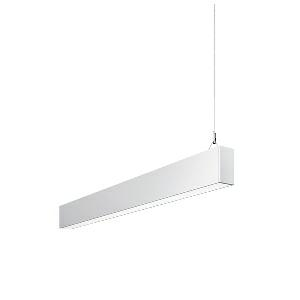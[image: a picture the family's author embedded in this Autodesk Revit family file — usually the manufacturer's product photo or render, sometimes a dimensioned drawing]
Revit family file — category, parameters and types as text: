
# Revit family: idoo_line_-_ilp_3000_vtl_d_end_00806451_e8ea
name_source: partatom
category: Lighting Fixtures
units: mm (PartAtom-declared; Revit-internal decimal feet)

## family parameters
Cut with Voids When Loaded = No
Host = Face
Light Source = No
Part Type = Normal
Room Calculation Point = No
Round Connector Dimension = Use Diameter
Shared = No

## types (1)
- IDOO.line - ILP 3000/VTL/D END (1 x LED, 3150 lm, 2700-6500K)
    Apparent Load = 32 VA
    Approval mark = CE
    CIE Flux Codes = 66 91 98 40 100
    Color Rendering = 90-100
    Color Temperature = 2700-6500K
    Control Gear = Electronic ballast
    Default Elevation = 1800 mm
    Description = ILP 3000/VTL/D|Suspended luminaire|light source: LED|connected load: 220-240 V, 50/60 Hz|Power consumption: approx. 32 W|standby: approx. 0,25|luminous flux: 3150 lm|luminous efficacy: 98 lm/W|light distribution: Direct/indirect|direct ratio: approx. 40 %|colour temperature: Cold white, ca. 2700-6500 K|color rendering index (CRI): >= 90|chromaticity tolerance:  3 SDCM|System of protection: IP 40|technology: Continuously dimmable|luminaire body|material: Sectional aluminium|colour: White|lamp cover: Acrylic (PMMA), Clear|mains lead: 1,0 m With free stranded wires|Fastening: Steel cable 0.3 - 0.7 m|glare control: Prism aperture|luminance(L65): <= 2700 cd/m|unified glare rating(4H 8H): <=  16|special features: Specified values at approx. 4000 K, DALI Load 1x, Through-wired, up to 18 m on one mains connection, External control required for Dali Device type 8, Flicker-free, Constant luminous flux between 2700 and 6500 K, Constant colour temperature over the whole dimming range, Suitable as emergency lighting, Mechanical and electrical connection of the individual modules without tools|
    Frequency = 50 Hz
    Height = 110 mm
    Lamp = 1 x LED
    Lamp Light Flux = 3150 lm
    Lamp count = 1
    Length = 1128 mm
    Luminous efficacy = 98 lm/W
    Manufacturer = Waldmann
    ModVariant = No
    Model = 00806451
    Mounting Place = Ceiling
    Mounting Type = Pendant
    Number of Poles = 1
    OnlyDefault = Yes
    Power Factor = 1
    Product Name = IDOO.line - ILP 3000/VTL/D END
    Product group = Suspended luminaire
    ProductGroupID = 9
    Protection Class = Protection class I
    Protection Degree = IP 40
    RLX_Detail_Level = 1
    RLX_Emergency_Light_Flux = 0 lm
    RLX_Emergency_Type = 0
    RLX_Emergency_Type_DB = No
    RlxData = <blob elided: 18517 chars, md5=d7ba9d4e>
    Socket = socket
    Standby Power = 0 W
    System Light Flux = 3150 lm
    System Power = 32 W
    Type Comments = Product without accessories
    Type Image = 113303000-00692573.jpg
    URL = http://relux.com
    VarID = ---
    Voltage = 230 V
    Voltage Range = 220-240 V
    Weight = 0.00 kg
    Width = 60 mm  [stored 0.19685 ft]

note: [stored X ft] marks values corroborated as IEEE doubles in the binary element streams (Revit-internal decimal feet)

## geometry (parser evidence)
native form markers: Blend x4, Sweep x13
no freeform markers — native parametric forms only
